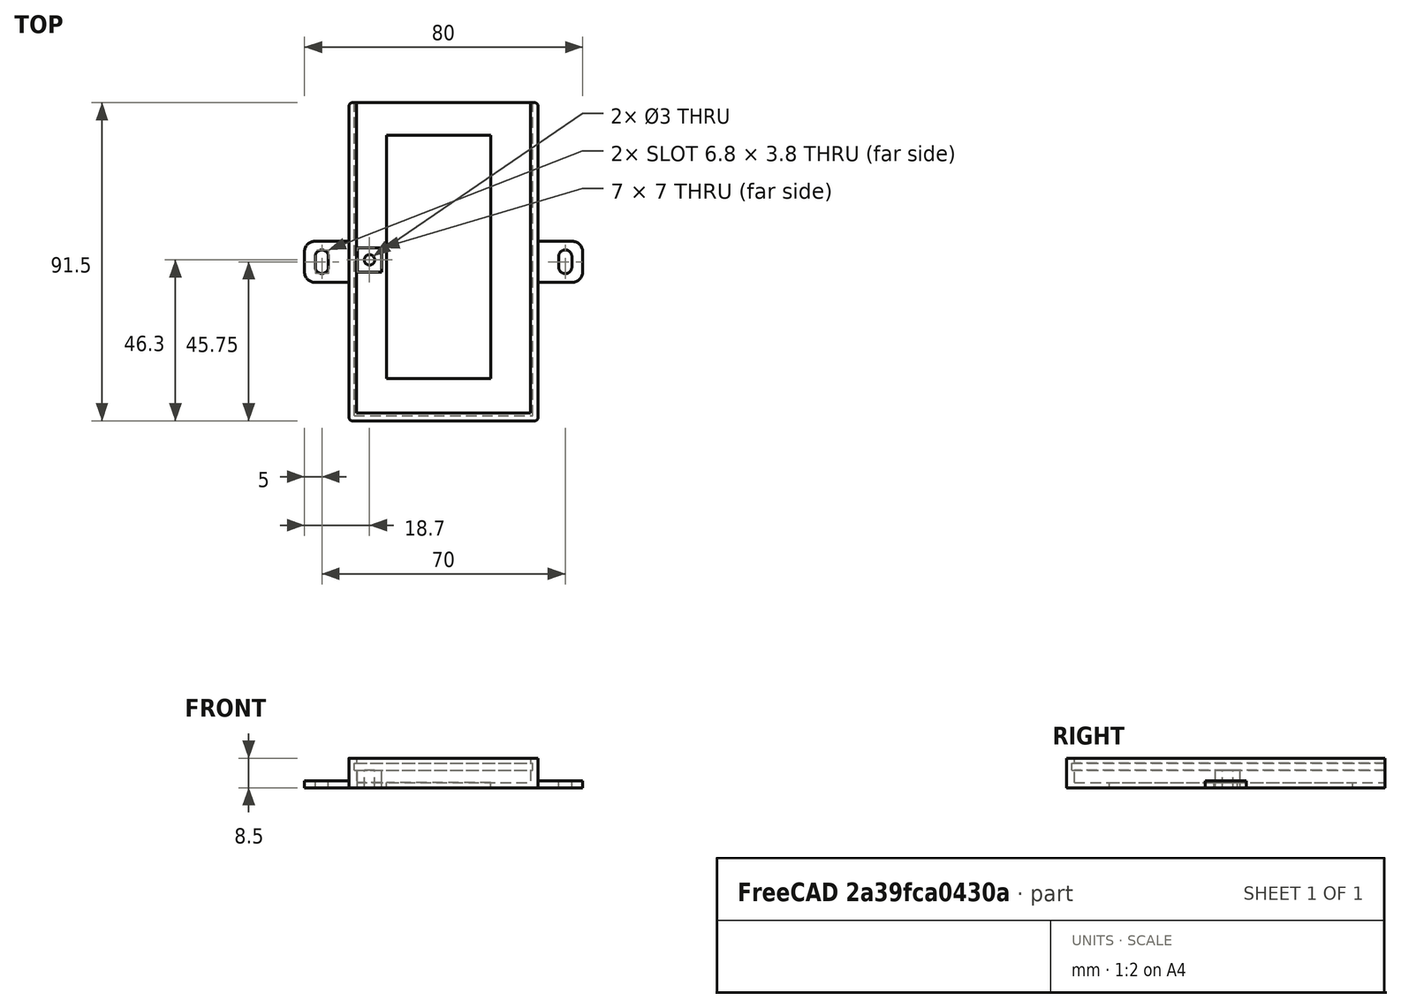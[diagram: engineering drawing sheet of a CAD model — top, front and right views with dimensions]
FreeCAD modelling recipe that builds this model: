
FCSTD DOCUMENT  (FreeCAD 0.19R23578 (Git))
Label: xilinx_linux_board
License: FreeArt
LicenseURL: http://artlibre.org/licence/lal
objects: Part::Box×5, Part::MultiFuse×4, Part::Cut×3, Spreadsheet::Sheet×1, Part::Fillet×1, Part::Cylinder×1, Part::Feature×1, App::Part×1
note: 15 computed .brp shape members not serialized (recipe doc carries the construction recipe); baked Part::Feature solids carry a one-line shape summary decoded from their .brp

FEATURE [Spreadsheet::Sheet] Spreadsheet  label="p"
  cells = A1=pcb_x; B1(pcb_x)=51.4; A2=pcb_y; B2(pcb_y)=90; A3=pcb_z; B3(pcb_z)=2; A4=pcb_under; B4(pcb_under)=3.5; A5=side_wall; B5(side_wall)=1.5; A6=pcb_side_lane; B6(pcb_side_lane)=0.7; A7=bottom_wall; B7(bottom_wall)=1.5; A8=pcb_above; B8(pcb_above)=1.5; A9=hole_r; B9(hole_r)=1.5; A10=hole_off_x; B10(hole_off_x)=4.4; A11=hole_off_y; B11(hole_off_y)=44.8; A12=hole_stand_size; B12(hole_stand_size)=7; A13=bottom_hole_size_x; B13(bottom_hole_size_x)=30; A14=bottom_hole_size_y; B14(bottom_hole_size_y)=70
FEATURE [Part::Box] Box  label="external cube"
  AttacherType = Attacher::AttachEngine3D
  Height = 8.5
  Length = 54.4
  Width = 91.5
  expr: Height = <<p>>.bottom_wall + <<p>>.pcb_under + <<p>>.pcb_z + <<p>>.pcb_above
  expr: Width = <<p>>.pcb_y + <<p>>.side_wall
  expr: Length = <<p>>.pcb_x + 2 * <<p>>.side_wall
FEATURE [Part::Box] Box006  label="internal cube"
  AttacherType = Attacher::AttachEngine3D
  Height = 7
  Length = 50
  Placement = pos=(2.2,2.2,1.5) rot=(0,0,1;0rad)
  Width = 90.1
  expr: .Placement.Base.y = <<p>>.side_wall + <<p>>.pcb_side_lane
  expr: .Placement.Base.x = <<p>>.side_wall + <<p>>.pcb_side_lane
  expr: .Placement.Base.z = <<p>>.bottom_wall
  expr: Height = <<p>>.pcb_under + <<p>>.pcb_z + <<p>>.pcb_above
  expr: Width = <<p>>.pcb_y - 2 * <<p>>.pcb_side_lane + <<p>>.side_wall
  expr: Length = <<p>>.pcb_x - 2 * <<p>>.pcb_side_lane
FEATURE [Part::Box] Box007  label="pcb extract cube"
  AttacherType = Attacher::AttachEngine3D
  Height = 2
  Length = 51.4
  Placement = pos=(1.5,1.5,5) rot=(0,0,1;0rad)
  Width = 90
  expr: .Placement.Base.y = <<p>>.side_wall
  expr: .Placement.Base.x = <<p>>.side_wall
  expr: Length = <<p>>.pcb_x
  expr: Width = <<p>>.pcb_y
  expr: .Placement.Base.z = <<p>>.bottom_wall + <<p>>.pcb_under
  expr: Height = <<p>>.pcb_z
FEATURE [Part::MultiFuse] Fusion  label="extract fusion"
  Shapes = -> [Box006,Box007]
FEATURE [Part::Fillet] Fillet  label="external fillet"
  Base = -> Box
  Edges = 4 edges r=1: [Edge1,Edge3,Edge5,Edge7]
FEATURE [Part::Cylinder] Cylinder  label="hole"
  Angle = 360
  AttacherType = Attacher::AttachEngine3D
  Height = 10
  Placement = pos=(5.9,46.3,0) rot=(0,0,1;0rad)
  Radius = 1.5
  expr: Radius = <<p>>.hole_r
  expr: .Placement.Base.x = <<p>>.hole_off_x + <<p>>.side_wall
  expr: .Placement.Base.y = <<p>>.hole_off_y + <<p>>.side_wall
FEATURE [Part::Box] Box008  label="stand"
  AttacherType = Attacher::AttachEngine3D
  Height = 5
  Length = 7
  Placement = pos=(2.4,42.8,0) rot=(0,0,1;0rad)
  Width = 7
  expr: Height = <<p>>.pcb_under + <<p>>.bottom_wall
  expr: Length = <<p>>.hole_stand_size
  expr: Width = <<p>>.hole_stand_size
  expr: .Placement.Base.x = <<p>>.hole_off_x - <<p>>.hole_stand_size / 2 + <<p>>.side_wall
  expr: .Placement.Base.y = <<p>>.hole_off_y - <<p>>.hole_stand_size / 2 + <<p>>.side_wall
FEATURE [Part::Cut] Cut003002  label="stand hole cut"
  Base = -> Box008
  Tool = -> Cylinder
FEATURE [Part::Box] Box009  label="hole cube"
  AttacherType = Attacher::AttachEngine3D
  Height = 10
  Length = 30
  Placement = pos=(10.75,12.2,0) rot=(0,0,1;0rad)
  Width = 70
  expr: Length = <<p>>.bottom_hole_size_x
  expr: Width = <<p>>.bottom_hole_size_y
  expr: .Placement.Base.y = (<<p>>.pcb_x + 2 * <<p>>.side_wall - <<p>>.bottom_hole_size_x) / 2
  expr: .Placement.Base.x = (<<p>>.pcb_y + <<p>>.side_wall - <<p>>.bottom_hole_size_y) / 2
FEATURE [Part::MultiFuse] Fusion003  label="hole fusion"
  Shapes = -> [Cylinder,Box009]
FEATURE [Part::Feature] Cut003004  label="attach plane x dir002"
  Placement = pos=(-12.8,39.85,0) rot=(0,0,1;0rad)
  shape: bbox 80 x 11.8 x 2 mm, 18 faces (baked)
FEATURE [Part::MultiFuse] Fusion001  label="body fusion"
  Shapes = -> [Fillet,Cut003004]
FEATURE [Part::Cut] Cut  label="body cut001"
  Base = -> Fusion001
  Tool = -> Fusion
FEATURE [Part::MultiFuse] Fusion002  label="mosfet fusion"
  Shapes = -> [Cut,Box008]
FEATURE [Part::Cut] Cut003003  label="body cut"
  Base = -> Fusion002
  Tool = -> Fusion003
FEATURE [App::Part] Part  label="xilinx linux board part"
  Group = -> [Box,Fillet,Fusion001,Fusion,Box007,Box006,Cut,Cylinder,Box008,Cut003002,Fusion002,Cut003003]
  Origin = -> Origin
